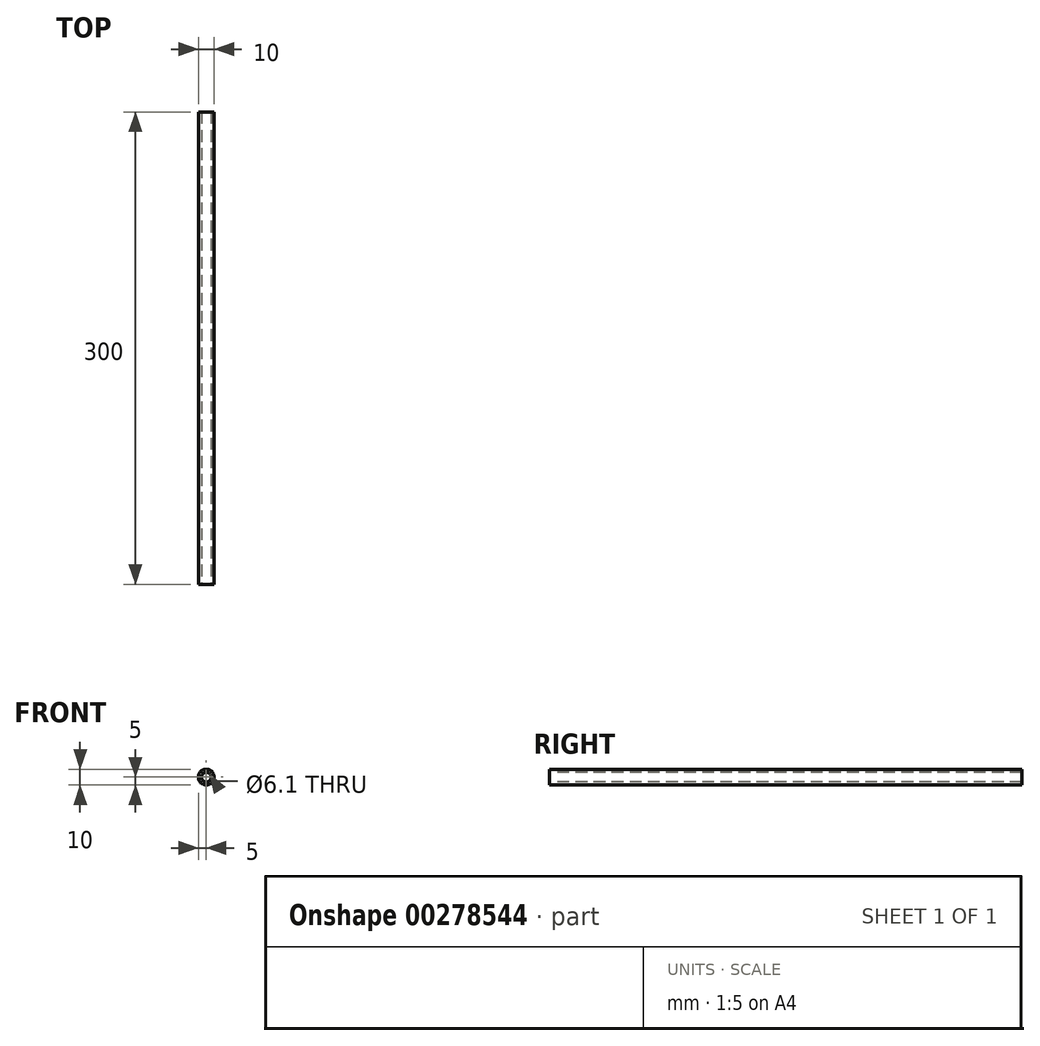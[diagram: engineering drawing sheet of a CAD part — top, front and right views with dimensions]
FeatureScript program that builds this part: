
annotation { "Feature Type Name" : "Feature", "Feature Type Description" : "" }
export const myFeature = defineFeature(function(context is Context, id is Id, definition is map)
    precondition{}
    {
        {
            var Q0;
            Q0=qCreatedBy(makeId("Front.planeOp"),FACE);
            var sketch = newSketch(context, id + "F0", { "sketchPlane" : qUnion([Q0])});
            skCircle(sketch, "E0", {"center": v(0, 0) * mm, "radius": 5 * mm});
            skSolve(sketch);
        }
        {
            var Q0;
            Q0 = qSketchRegion(id + "F0", true);
            extrude(context, id + "F1", {"entities" : qUnion([Q0]), "depth" : 300 * mm});
        }
        {
            var Q0;
            Q0=makeQuery(id+"F1.opExtrude","CAP_FACE",FACE,{"disambiguationData":[OSD([sQuery(id+"F0.wireOp",EDGE,"E0")])],"isStart":false});
            var sketch = newSketch(context, id + "F2", { "sketchPlane" : qUnion([Q0])});
            skCircle(sketch, "E1", {"center": v(0, 0) * mm, "radius": 3.05 * mm});
            skSolve(sketch);
        }
        {
            var Q0;
            Q0=makeQuery(id+"F2.imprint","IMPRINT",FACE,{"disambiguationData":[TD([[makeQuery(id+"F2.imprint","IMPRINT",EDGE,{"derivedFrom":sQuery(id+"F2.wireOp",EDGE,"E1")}),1.0]])]});
            var Q1;
            Q1=sQuery(id+"F2.wireOp",EDGE,"E1");
            extrude(context, id + "F3", {"entities" : qUnion([Q0]), "operationType" : NewBodyOperationType.REMOVE, "surfaceEntities" : qUnion([Q1]), "endBound" : BoundingType.THROUGH_ALL, "oppositeDirection" : true, "depth" : 25 * mm});
        }
    });
